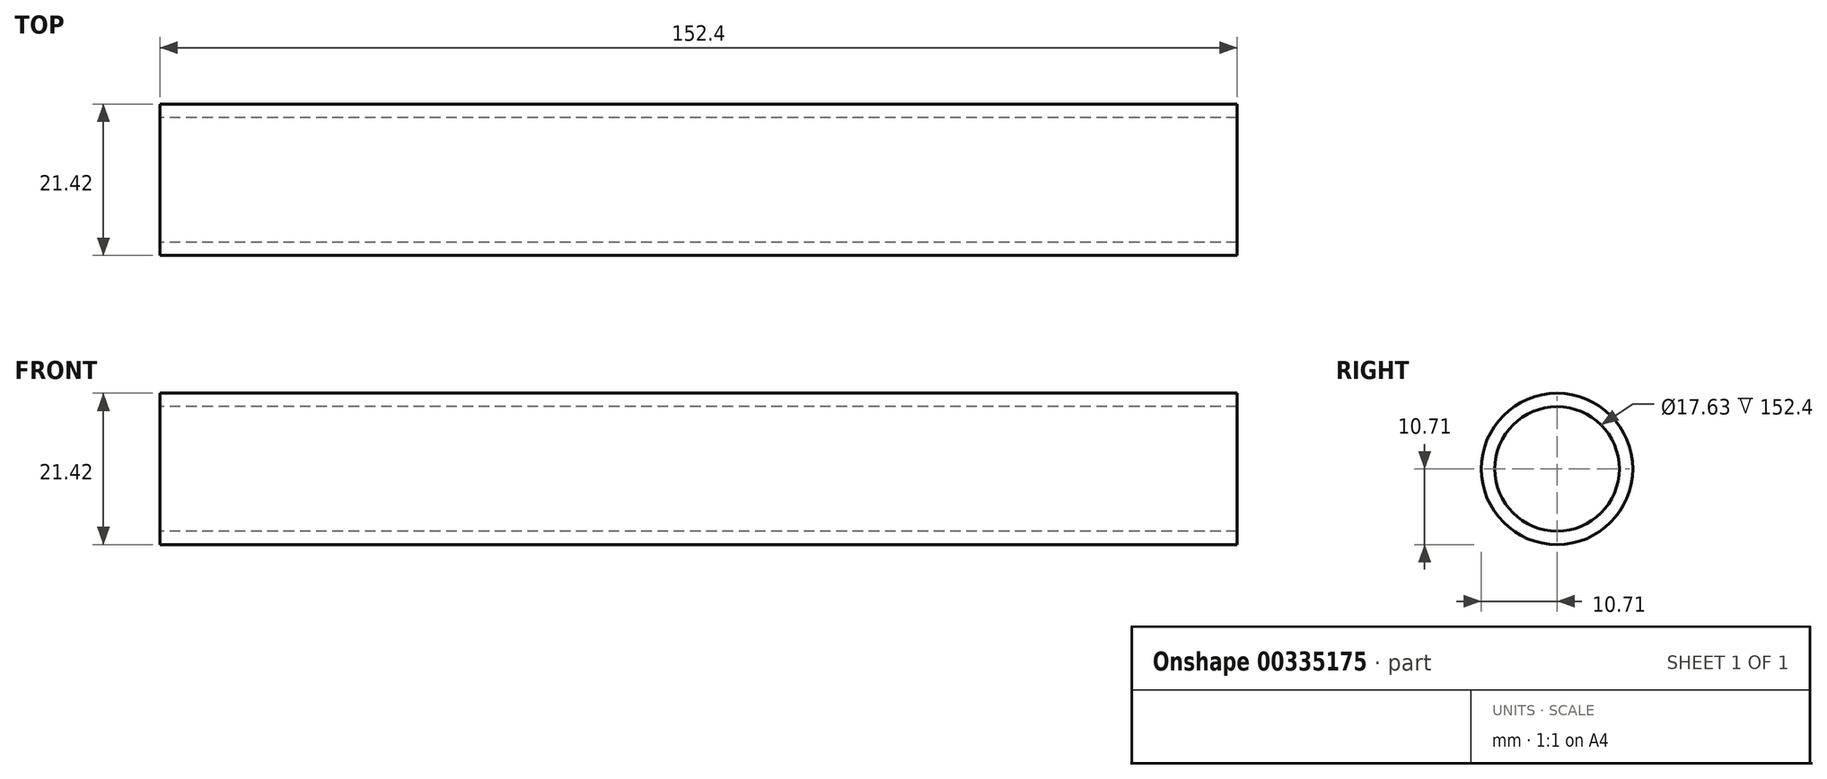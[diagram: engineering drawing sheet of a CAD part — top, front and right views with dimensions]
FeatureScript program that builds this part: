
annotation { "Feature Type Name" : "Feature", "Feature Type Description" : "" }
export const myFeature = defineFeature(function(context is Context, id is Id, definition is map)
    precondition{}
    {
        {
            var Q0;
            Q0=qCreatedBy(makeId("Right.planeOp"),FACE);
            var sketch = newSketch(context, id + "F0", { "sketchPlane" : qUnion([Q0])});
            skCircle(sketch, "E0", {"center": v(0, 0) * mm, "radius": 8.81 * mm});
            skCircle(sketch, "E1", {"center": v(0, 0) * mm, "radius": 10.7 * mm});
            skSolve(sketch);
        }
        {
            var Q0;
            Q0 = qSketchRegion(id + "F0", true);
            extrude(context, id + "F1", {"entities" : qUnion([Q0]), "depth" : 152.4 * mm});
        }
    });
